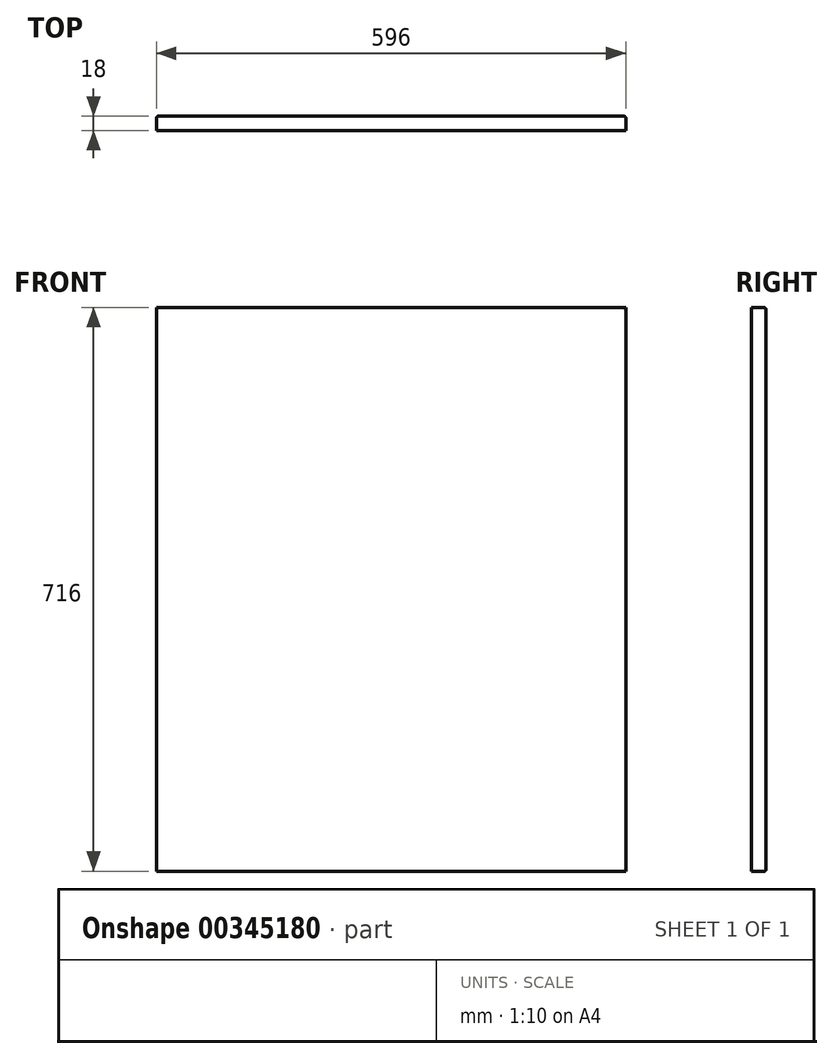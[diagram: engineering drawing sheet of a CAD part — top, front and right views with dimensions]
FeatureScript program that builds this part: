
annotation { "Feature Type Name" : "Feature", "Feature Type Description" : "" }
export const myFeature = defineFeature(function(context is Context, id is Id, definition is map)
    precondition{}
    {
        {
            var Q0;
            Q0=qCreatedBy(makeId("Front.planeOp"),FACE);
            var sketch = newSketch(context, id + "F0", { "sketchPlane" : qUnion([Q0])});
            skLineSegment(sketch, "E0.bottom", {"start": v(0, 0) * mm, "end": v(-39.7, 0) * mm});
            skLineSegment(sketch, "E0.top", {"start": v(0, 31.03) * mm, "end": v(-39.7, 31.03) * mm});
            skLineSegment(sketch, "E0.left", {"start": v(0, 0) * mm, "end": v(0, 31.03) * mm});
            skLineSegment(sketch, "E0.right", {"start": v(-39.7, 0) * mm, "end": v(-39.7, 31.03) * mm});
            skSolve(sketch);
        }
        {
            var Q0;
            Q0=makeQuery(id+"F0.imprint","IMPRINT",FACE,{"disambiguationData":[TD([[makeQuery(id+"F0.imprint","IMPRINT",EDGE,{"derivedFrom":sQuery(id+"F0.wireOp",EDGE,"E0.bottom")}),-1.0]])]});
            extrude(context, id + "F1", {"entities" : qUnion([Q0]), "oppositeDirection" : true, "depth" : 18 * mm});
        }
        {
            var Q0;
            Q0=makeQuery(id+"F1.opExtrude","SWEPT_FACE",FACE,{"disambiguationData":[OSD([sQuery(id+"F0.wireOp",EDGE,"E0.bottom")])]});
            extrude(context, id + "F2", {"entities" : qUnion([Q0]), "operationType" : NewBodyOperationType.ADD, "oppositeDirection" : true, "depth" : 716 * mm});
        }
        {
            var Q0;
            {var subQ0=sQuery(id+"F0.wireOp",EDGE,"E0.left");Q0=makeQuery(id+"F2.boolean.opBoolean","MERGE",FACE,{"derivedFrom":[makeQuery(id+"F1.opExtrude","SWEPT_FACE",FACE,{"disambiguationData":[OSD([subQ0])]}),makeQuery(id+"F2.opExtrude","SWEPT_FACE",FACE,{"disambiguationData":[OSD([sQuery(id+"F0.wireOp",EDGE,"E0.bottom"),subQ0])]})]});}
            extrude(context, id + "F3", {"entities" : qUnion([Q0]), "operationType" : NewBodyOperationType.ADD, "oppositeDirection" : true, "depth" : 596 * mm});
        }
        {
            var Q0;
            {var subQ0=sQuery(id+"F0.wireOp",EDGE,"E0.left");var subQ1=sQuery(id+"F0.wireOp",EDGE,"E0.bottom");Q0=makeQuery(id+"F3.boolean.opBoolean","MERGE",FACE,{"derivedFrom":[makeQuery(id+"F2.boolean.opBoolean","MERGE",FACE,{"derivedFrom":[makeQuery(id+"F1.opExtrude","CAP_FACE",FACE,{"disambiguationData":[OSD([subQ1,sQuery(id+"F0.wireOp",EDGE,"E0.top"),subQ0,sQuery(id+"F0.wireOp",EDGE,"E0.right")])],"isStart":false}),makeQuery(id+"F2.opExtrude","SWEPT_FACE",FACE,{"disambiguationData":[OSD([subQ1]),TDD([makeQuery(id+"F1.opExtrude","CAP_EDGE",EDGE,{"disambiguationData":[OSD([subQ1])],"isStart":false})])]})]}),makeQuery(id+"F3.opExtrude","SWEPT_FACE",FACE,{"disambiguationData":[OSD([subQ1,subQ0]),TDD([makeQuery(id+"F2.boolean.opBoolean","MERGE",EDGE,{"derivedFrom":[makeQuery(id+"F1.opExtrude","CAP_EDGE",EDGE,{"disambiguationData":[OSD([subQ0])],"isStart":false}),makeQuery(id+"F2.opExtrude","SWEPT_EDGE",EDGE,{"disambiguationData":[OSD([subQ1,subQ0]),TDD([makeQuery(id+"F1.opExtrude","CAP_VERTEX",VERTEX,{"disambiguationData":[OSD([subQ1,subQ0])],"isStart":false})])]})]})])]})]});}
            fillet(context, id + "F4", {"entities" : qUnion([Q0]), "radius" : 2 * mm, "tangentPropagation" : true, "allowEdgeOverflow" : false});
        }
    });
